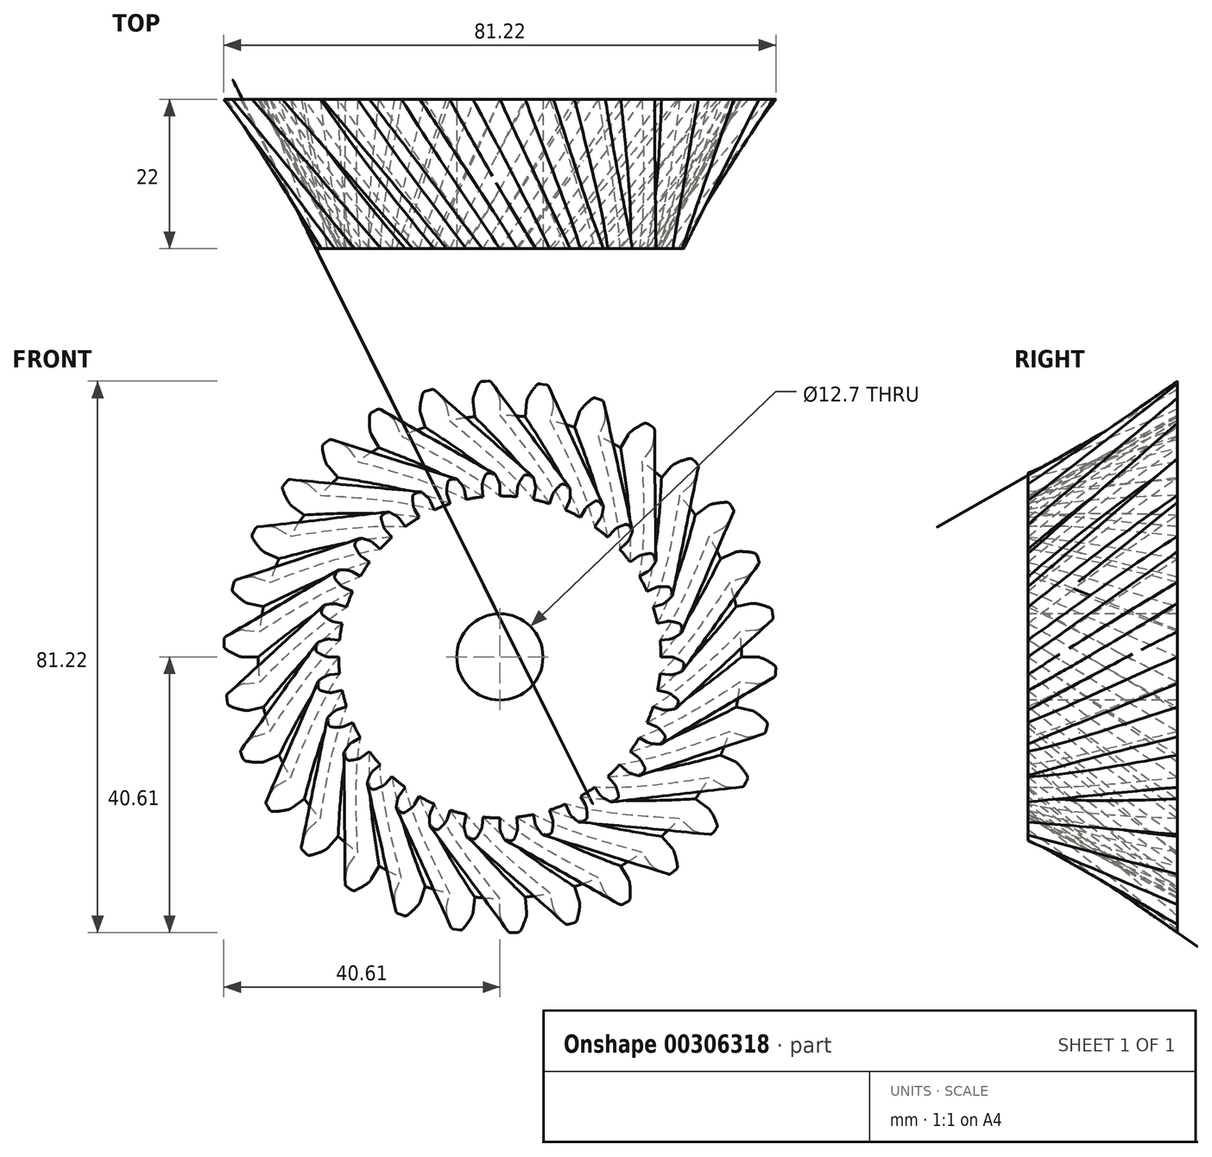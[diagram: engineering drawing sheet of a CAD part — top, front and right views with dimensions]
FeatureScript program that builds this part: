
annotation { "Feature Type Name" : "Feature", "Feature Type Description" : "" }
export const myFeature = defineFeature(function(context is Context, id is Id, definition is map)
    precondition{}
    {
        {
            var Q0;
            Q0=qCreatedBy(makeId("Front.planeOp"),FACE);
            var sketch = newSketch(context, id + "F0", { "sketchPlane" : qUnion([Q0])});
            skCircle(sketch, "E0", {"center": v(0, 0) * mm, "radius": 35.56 * mm});
            skArc(sketch, "E1.trimOffspring", {"start": v(-0.11, 38.4) * mm, "mid": v(-0.6, 39.43) * mm, "end": v(-1.21, 40.4) * mm});
            skLineSegment(sketch, "E2", {"start": v(0, 37.8) * mm, "end": v(0, 35.56) * mm});
            skLineSegment(sketch, "E3", {"start": v(-1.64, 40.6) * mm, "end": v(-2.13, 40.6) * mm});
            skLineSegment(sketch, "E4.MirrorCS", {"start": v(-2.61, 40.56) * mm, "end": v(-2.13, 40.6) * mm});
            skArc(sketch, "E5.MirrorCS", {"start": v(-3.9, 38.2) * mm, "mid": v(-3.52, 39.28) * mm, "end": v(-3.02, 40.3) * mm});
            skLineSegment(sketch, "E6.MirrorCS", {"start": v(-3.95, 37.6) * mm, "end": v(-3.72, 35.37) * mm});
            skPoint(sketch, "E7.visualSharp", {"position": v(-3.98, 37.9) * mm});
            skArc(sketch, "E7.filletArc", {"start": v(-3.9, 38.2) * mm, "mid": v(-3.95, 37.9) * mm, "end": v(-3.95, 37.6) * mm});
            skPoint(sketch, "E8.visualSharp", {"position": v(0, 38.1) * mm});
            skArc(sketch, "E8.filletArc", {"start": v(0, 37.8) * mm, "mid": v(-0.03, 38.1) * mm, "end": v(-0.11, 38.4) * mm});
            skPoint(sketch, "E9.visualSharp", {"position": v(-2.88, 40.54) * mm});
            skArc(sketch, "E9.filletArc", {"start": v(-2.61, 40.56) * mm, "mid": v(-2.85, 40.48) * mm, "end": v(-3.02, 40.3) * mm});
            skPoint(sketch, "E10.visualSharp", {"position": v(-1.38, 40.62) * mm});
            skArc(sketch, "E10.filletArc", {"start": v(-1.21, 40.4) * mm, "mid": v(-1.4, 40.56) * mm, "end": v(-1.64, 40.6) * mm});
            skLineSegment(sketch, "E11.1.0", {"start": v(-11.68, 35.96) * mm, "end": v(-10.99, 33.82) * mm});
            skArc(sketch, "E11.1.1", {"start": v(-11.76, 36.56) * mm, "mid": v(-11.75, 36.25) * mm, "end": v(-11.68, 35.96) * mm});
            skArc(sketch, "E11.1.2", {"start": v(-11.76, 36.56) * mm, "mid": v(-11.61, 37.69) * mm, "end": v(-11.33, 38.8) * mm});
            skArc(sketch, "E11.1.3", {"start": v(-10.99, 39.13) * mm, "mid": v(-11.2, 39) * mm, "end": v(-11.33, 38.8) * mm});
            skLineSegment(sketch, "E11.1.4", {"start": v(-10.99, 39.13) * mm, "end": v(-10.52, 39.26) * mm});
            skLineSegment(sketch, "E11.1.5", {"start": v(-10.05, 39.38) * mm, "end": v(-10.52, 39.26) * mm});
            skArc(sketch, "E11.1.6", {"start": v(-9.58, 39.26) * mm, "mid": v(-9.8, 39.38) * mm, "end": v(-10.05, 39.38) * mm});
            skArc(sketch, "E11.1.7", {"start": v(-8.1, 37.54) * mm, "mid": v(-8.79, 38.44) * mm, "end": v(-9.58, 39.26) * mm});
            skArc(sketch, "E11.1.8", {"start": v(-7.86, 36.98) * mm, "mid": v(-7.95, 37.27) * mm, "end": v(-8.1, 37.54) * mm});
            skLineSegment(sketch, "E11.1.9", {"start": v(-7.86, 36.98) * mm, "end": v(-7.4, 34.78) * mm});
            skLineSegment(sketch, "E11.2.0", {"start": v(-18.9, 32.74) * mm, "end": v(-17.78, 30.8) * mm});
            skArc(sketch, "E11.2.1", {"start": v(-19.1, 33.31) * mm, "mid": v(-19.03, 33.02) * mm, "end": v(-18.9, 32.74) * mm});
            skArc(sketch, "E11.2.2", {"start": v(-19.1, 33.31) * mm, "mid": v(-19.2, 34.45) * mm, "end": v(-19.15, 35.6) * mm});
            skArc(sketch, "E11.2.3", {"start": v(-18.88, 35.99) * mm, "mid": v(-19.06, 35.82) * mm, "end": v(-19.15, 35.6) * mm});
            skLineSegment(sketch, "E11.2.4", {"start": v(-18.88, 35.99) * mm, "end": v(-18.45, 36.22) * mm});
            skLineSegment(sketch, "E11.2.5", {"start": v(-18.02, 36.43) * mm, "end": v(-18.45, 36.22) * mm});
            skArc(sketch, "E11.2.6", {"start": v(-17.54, 36.41) * mm, "mid": v(-17.78, 36.48) * mm, "end": v(-18.02, 36.43) * mm});
            skArc(sketch, "E11.2.7", {"start": v(-15.72, 35.03) * mm, "mid": v(-16.59, 35.78) * mm, "end": v(-17.54, 36.41) * mm});
            skArc(sketch, "E11.2.8", {"start": v(-15.38, 34.54) * mm, "mid": v(-15.53, 34.8) * mm, "end": v(-15.72, 35.03) * mm});
            skLineSegment(sketch, "E11.2.9", {"start": v(-15.38, 34.54) * mm, "end": v(-14.46, 32.49) * mm});
            skLineSegment(sketch, "E11.3.0", {"start": v(-25.3, 28.1) * mm, "end": v(-23.8, 26.43) * mm});
            skArc(sketch, "E11.3.1", {"start": v(-25.6, 28.61) * mm, "mid": v(-25.48, 28.34) * mm, "end": v(-25.3, 28.1) * mm});
            skArc(sketch, "E11.3.2", {"start": v(-25.6, 28.61) * mm, "mid": v(-25.94, 29.7) * mm, "end": v(-26.13, 30.83) * mm});
            skArc(sketch, "E11.3.3", {"start": v(-25.95, 31.28) * mm, "mid": v(-26.1, 31.08) * mm, "end": v(-26.13, 30.83) * mm});
            skLineSegment(sketch, "E11.3.4", {"start": v(-25.95, 31.28) * mm, "end": v(-25.58, 31.59) * mm});
            skLineSegment(sketch, "E11.3.5", {"start": v(-25.2, 31.89) * mm, "end": v(-25.58, 31.59) * mm});
            skArc(sketch, "E11.3.6", {"start": v(-24.73, 31.97) * mm, "mid": v(-24.97, 31.99) * mm, "end": v(-25.2, 31.89) * mm});
            skArc(sketch, "E11.3.7", {"start": v(-22.66, 31) * mm, "mid": v(-23.67, 31.55) * mm, "end": v(-24.73, 31.97) * mm});
            skArc(sketch, "E11.3.8", {"start": v(-22.22, 30.59) * mm, "mid": v(-22.42, 30.81) * mm, "end": v(-22.66, 31) * mm});
            skLineSegment(sketch, "E11.3.9", {"start": v(-22.22, 30.59) * mm, "end": v(-20.9, 28.77) * mm});
            skLineSegment(sketch, "E11.4.0", {"start": v(-30.59, 22.22) * mm, "end": v(-28.77, 20.9) * mm});
            skArc(sketch, "E11.4.1", {"start": v(-31, 22.66) * mm, "mid": v(-30.81, 22.42) * mm, "end": v(-30.59, 22.22) * mm});
            skArc(sketch, "E11.4.2", {"start": v(-31, 22.66) * mm, "mid": v(-31.55, 23.67) * mm, "end": v(-31.97, 24.73) * mm});
            skArc(sketch, "E11.4.3", {"start": v(-31.89, 25.2) * mm, "mid": v(-31.99, 24.97) * mm, "end": v(-31.97, 24.73) * mm});
            skLineSegment(sketch, "E11.4.4", {"start": v(-31.89, 25.2) * mm, "end": v(-31.59, 25.58) * mm});
            skLineSegment(sketch, "E11.4.5", {"start": v(-31.28, 25.95) * mm, "end": v(-31.59, 25.58) * mm});
            skArc(sketch, "E11.4.6", {"start": v(-30.83, 26.13) * mm, "mid": v(-31.08, 26.1) * mm, "end": v(-31.28, 25.95) * mm});
            skArc(sketch, "E11.4.7", {"start": v(-28.61, 25.6) * mm, "mid": v(-29.7, 25.94) * mm, "end": v(-30.83, 26.13) * mm});
            skArc(sketch, "E11.4.8", {"start": v(-28.1, 25.3) * mm, "mid": v(-28.34, 25.48) * mm, "end": v(-28.61, 25.6) * mm});
            skLineSegment(sketch, "E11.4.9", {"start": v(-28.1, 25.3) * mm, "end": v(-26.43, 23.8) * mm});
            skLineSegment(sketch, "E11.5.0", {"start": v(-34.54, 15.38) * mm, "end": v(-32.49, 14.46) * mm});
            skArc(sketch, "E11.5.1", {"start": v(-35.03, 15.72) * mm, "mid": v(-34.8, 15.53) * mm, "end": v(-34.54, 15.38) * mm});
            skArc(sketch, "E11.5.2", {"start": v(-35.03, 15.72) * mm, "mid": v(-35.78, 16.59) * mm, "end": v(-36.41, 17.54) * mm});
            skArc(sketch, "E11.5.3", {"start": v(-36.43, 18.02) * mm, "mid": v(-36.48, 17.78) * mm, "end": v(-36.41, 17.54) * mm});
            skLineSegment(sketch, "E11.5.4", {"start": v(-36.43, 18.02) * mm, "end": v(-36.22, 18.45) * mm});
            skLineSegment(sketch, "E11.5.5", {"start": v(-35.99, 18.88) * mm, "end": v(-36.22, 18.45) * mm});
            skArc(sketch, "E11.5.6", {"start": v(-35.6, 19.15) * mm, "mid": v(-35.82, 19.06) * mm, "end": v(-35.99, 18.88) * mm});
            skArc(sketch, "E11.5.7", {"start": v(-33.31, 19.1) * mm, "mid": v(-34.45, 19.2) * mm, "end": v(-35.6, 19.15) * mm});
            skArc(sketch, "E11.5.8", {"start": v(-32.74, 18.9) * mm, "mid": v(-33.02, 19.03) * mm, "end": v(-33.31, 19.1) * mm});
            skLineSegment(sketch, "E11.5.9", {"start": v(-32.74, 18.9) * mm, "end": v(-30.8, 17.78) * mm});
            skLineSegment(sketch, "E11.6.0", {"start": v(-36.98, 7.86) * mm, "end": v(-34.78, 7.4) * mm});
            skArc(sketch, "E11.6.1", {"start": v(-37.54, 8.1) * mm, "mid": v(-37.27, 7.95) * mm, "end": v(-36.98, 7.86) * mm});
            skArc(sketch, "E11.6.2", {"start": v(-37.54, 8.1) * mm, "mid": v(-38.44, 8.79) * mm, "end": v(-39.26, 9.58) * mm});
            skArc(sketch, "E11.6.3", {"start": v(-39.38, 10.05) * mm, "mid": v(-39.38, 9.8) * mm, "end": v(-39.26, 9.58) * mm});
            skLineSegment(sketch, "E11.6.4", {"start": v(-39.38, 10.05) * mm, "end": v(-39.26, 10.52) * mm});
            skLineSegment(sketch, "E11.6.5", {"start": v(-39.13, 10.99) * mm, "end": v(-39.26, 10.52) * mm});
            skArc(sketch, "E11.6.6", {"start": v(-38.8, 11.33) * mm, "mid": v(-39, 11.2) * mm, "end": v(-39.13, 10.99) * mm});
            skArc(sketch, "E11.6.7", {"start": v(-36.56, 11.76) * mm, "mid": v(-37.69, 11.61) * mm, "end": v(-38.8, 11.33) * mm});
            skArc(sketch, "E11.6.8", {"start": v(-35.96, 11.68) * mm, "mid": v(-36.25, 11.75) * mm, "end": v(-36.56, 11.76) * mm});
            skLineSegment(sketch, "E11.6.9", {"start": v(-35.96, 11.68) * mm, "end": v(-33.82, 10.99) * mm});
            skLineSegment(sketch, "E11.7.0", {"start": v(-37.8, 0) * mm, "end": v(-35.56, 0) * mm});
            skArc(sketch, "E11.7.1", {"start": v(-38.4, 0.11) * mm, "mid": v(-38.1, 0.03) * mm, "end": v(-37.8, 0) * mm});
            skArc(sketch, "E11.7.2", {"start": v(-38.4, 0.11) * mm, "mid": v(-39.43, 0.6) * mm, "end": v(-40.4, 1.21) * mm});
            skArc(sketch, "E11.7.3", {"start": v(-40.6, 1.64) * mm, "mid": v(-40.56, 1.4) * mm, "end": v(-40.4, 1.21) * mm});
            skLineSegment(sketch, "E11.7.4", {"start": v(-40.6, 1.64) * mm, "end": v(-40.6, 2.13) * mm});
            skLineSegment(sketch, "E11.7.5", {"start": v(-40.56, 2.61) * mm, "end": v(-40.6, 2.13) * mm});
            skArc(sketch, "E11.7.6", {"start": v(-40.3, 3.02) * mm, "mid": v(-40.48, 2.85) * mm, "end": v(-40.56, 2.61) * mm});
            skArc(sketch, "E11.7.7", {"start": v(-38.2, 3.9) * mm, "mid": v(-39.28, 3.52) * mm, "end": v(-40.3, 3.02) * mm});
            skArc(sketch, "E11.7.8", {"start": v(-37.6, 3.95) * mm, "mid": v(-37.9, 3.95) * mm, "end": v(-38.2, 3.9) * mm});
            skLineSegment(sketch, "E11.7.9", {"start": v(-37.6, 3.95) * mm, "end": v(-35.37, 3.72) * mm});
            skLineSegment(sketch, "E11.8.0", {"start": v(-36.98, -7.86) * mm, "end": v(-34.78, -7.4) * mm});
            skArc(sketch, "E11.8.1", {"start": v(-37.58, -7.87) * mm, "mid": v(-37.28, -7.9) * mm, "end": v(-36.98, -7.86) * mm});
            skArc(sketch, "E11.8.2", {"start": v(-37.58, -7.87) * mm, "mid": v(-38.7, -7.6) * mm, "end": v(-39.77, -7.21) * mm});
            skArc(sketch, "E11.8.3", {"start": v(-40.06, -6.84) * mm, "mid": v(-39.96, -7.06) * mm, "end": v(-39.77, -7.21) * mm});
            skLineSegment(sketch, "E11.8.4", {"start": v(-40.06, -6.84) * mm, "end": v(-40.15, -6.36) * mm});
            skLineSegment(sketch, "E11.8.5", {"start": v(-40.21, -5.88) * mm, "end": v(-40.15, -6.36) * mm});
            skArc(sketch, "E11.8.6", {"start": v(-40.05, -5.43) * mm, "mid": v(-40.19, -5.63) * mm, "end": v(-40.21, -5.88) * mm});
            skArc(sketch, "E11.8.7", {"start": v(-38.18, -4.13) * mm, "mid": v(-39.15, -4.72) * mm, "end": v(-40.05, -5.43) * mm});
            skArc(sketch, "E11.8.8", {"start": v(-37.6, -3.95) * mm, "mid": v(-37.9, -4.01) * mm, "end": v(-38.18, -4.13) * mm});
            skLineSegment(sketch, "E11.8.9", {"start": v(-37.6, -3.95) * mm, "end": v(-35.37, -3.72) * mm});
            skLineSegment(sketch, "E11.9.0", {"start": v(-34.54, -15.38) * mm, "end": v(-32.49, -14.46) * mm});
            skArc(sketch, "E11.9.1", {"start": v(-35.13, -15.51) * mm, "mid": v(-34.83, -15.47) * mm, "end": v(-34.54, -15.38) * mm});
            skArc(sketch, "E11.9.2", {"start": v(-35.13, -15.51) * mm, "mid": v(-36.27, -15.49) * mm, "end": v(-37.4, -15.32) * mm});
            skArc(sketch, "E11.9.3", {"start": v(-37.76, -15.02) * mm, "mid": v(-37.62, -15.22) * mm, "end": v(-37.4, -15.32) * mm});
            skLineSegment(sketch, "E11.9.4", {"start": v(-37.76, -15.02) * mm, "end": v(-37.95, -14.57) * mm});
            skLineSegment(sketch, "E11.9.5", {"start": v(-38.11, -14.11) * mm, "end": v(-37.95, -14.57) * mm});
            skArc(sketch, "E11.9.6", {"start": v(-38.04, -13.64) * mm, "mid": v(-38.14, -13.86) * mm, "end": v(-38.11, -14.11) * mm});
            skArc(sketch, "E11.9.7", {"start": v(-36.48, -11.98) * mm, "mid": v(-37.31, -12.76) * mm, "end": v(-38.04, -13.64) * mm});
            skArc(sketch, "E11.9.8", {"start": v(-35.96, -11.68) * mm, "mid": v(-36.23, -11.8) * mm, "end": v(-36.48, -11.98) * mm});
            skLineSegment(sketch, "E11.9.9", {"start": v(-35.96, -11.68) * mm, "end": v(-33.82, -10.99) * mm});
            skLineSegment(sketch, "E11.10.0", {"start": v(-30.59, -22.22) * mm, "end": v(-28.77, -20.9) * mm});
            skArc(sketch, "E11.10.1", {"start": v(-31.13, -22.48) * mm, "mid": v(-30.85, -22.38) * mm, "end": v(-30.59, -22.22) * mm});
            skArc(sketch, "E11.10.2", {"start": v(-31.13, -22.48) * mm, "mid": v(-32.26, -22.69) * mm, "end": v(-33.4, -22.76) * mm});
            skArc(sketch, "E11.10.3", {"start": v(-33.82, -22.54) * mm, "mid": v(-33.63, -22.7) * mm, "end": v(-33.4, -22.76) * mm});
            skLineSegment(sketch, "E11.10.4", {"start": v(-33.82, -22.54) * mm, "end": v(-34.09, -22.14) * mm});
            skLineSegment(sketch, "E11.10.5", {"start": v(-34.35, -21.73) * mm, "end": v(-34.09, -22.14) * mm});
            skArc(sketch, "E11.10.6", {"start": v(-34.38, -21.25) * mm, "mid": v(-34.42, -21.5) * mm, "end": v(-34.35, -21.73) * mm});
            skArc(sketch, "E11.10.7", {"start": v(-33.2, -19.3) * mm, "mid": v(-33.85, -20.24) * mm, "end": v(-34.38, -21.25) * mm});
            skArc(sketch, "E11.10.8", {"start": v(-32.74, -18.9) * mm, "mid": v(-32.99, -19.08) * mm, "end": v(-33.2, -19.3) * mm});
            skLineSegment(sketch, "E11.10.9", {"start": v(-32.74, -18.9) * mm, "end": v(-30.8, -17.78) * mm});
            skLineSegment(sketch, "E11.11.0", {"start": v(-25.3, -28.1) * mm, "end": v(-23.8, -26.43) * mm});
            skArc(sketch, "E11.11.1", {"start": v(-25.78, -28.46) * mm, "mid": v(-25.52, -28.3) * mm, "end": v(-25.3, -28.1) * mm});
            skArc(sketch, "E11.11.2", {"start": v(-25.78, -28.46) * mm, "mid": v(-26.83, -28.9) * mm, "end": v(-27.93, -29.2) * mm});
            skArc(sketch, "E11.11.3", {"start": v(-28.4, -29.08) * mm, "mid": v(-28.18, -29.2) * mm, "end": v(-27.93, -29.2) * mm});
            skLineSegment(sketch, "E11.11.4", {"start": v(-28.4, -29.08) * mm, "end": v(-28.74, -28.74) * mm});
            skLineSegment(sketch, "E11.11.5", {"start": v(-29.08, -28.4) * mm, "end": v(-28.74, -28.74) * mm});
            skArc(sketch, "E11.11.6", {"start": v(-29.2, -27.93) * mm, "mid": v(-29.2, -28.18) * mm, "end": v(-29.08, -28.4) * mm});
            skArc(sketch, "E11.11.7", {"start": v(-28.46, -25.78) * mm, "mid": v(-28.9, -26.83) * mm, "end": v(-29.2, -27.93) * mm});
            skArc(sketch, "E11.11.8", {"start": v(-28.1, -25.3) * mm, "mid": v(-28.3, -25.52) * mm, "end": v(-28.46, -25.78) * mm});
            skLineSegment(sketch, "E11.11.9", {"start": v(-28.1, -25.3) * mm, "end": v(-26.43, -23.8) * mm});
            skLineSegment(sketch, "E11.12.0", {"start": v(-18.9, -32.74) * mm, "end": v(-17.78, -30.8) * mm});
            skArc(sketch, "E11.12.1", {"start": v(-19.3, -33.2) * mm, "mid": v(-19.08, -32.99) * mm, "end": v(-18.9, -32.74) * mm});
            skArc(sketch, "E11.12.2", {"start": v(-19.3, -33.2) * mm, "mid": v(-20.24, -33.85) * mm, "end": v(-21.25, -34.38) * mm});
            skArc(sketch, "E11.12.3", {"start": v(-21.73, -34.35) * mm, "mid": v(-21.5, -34.42) * mm, "end": v(-21.25, -34.38) * mm});
            skLineSegment(sketch, "E11.12.4", {"start": v(-21.73, -34.35) * mm, "end": v(-22.14, -34.09) * mm});
            skLineSegment(sketch, "E11.12.5", {"start": v(-22.54, -33.82) * mm, "end": v(-22.14, -34.09) * mm});
            skArc(sketch, "E11.12.6", {"start": v(-22.76, -33.4) * mm, "mid": v(-22.7, -33.63) * mm, "end": v(-22.54, -33.82) * mm});
            skArc(sketch, "E11.12.7", {"start": v(-22.48, -31.13) * mm, "mid": v(-22.69, -32.26) * mm, "end": v(-22.76, -33.4) * mm});
            skArc(sketch, "E11.12.8", {"start": v(-22.22, -30.59) * mm, "mid": v(-22.38, -30.85) * mm, "end": v(-22.48, -31.13) * mm});
            skLineSegment(sketch, "E11.12.9", {"start": v(-22.22, -30.59) * mm, "end": v(-20.9, -28.77) * mm});
            skLineSegment(sketch, "E11.13.0", {"start": v(-11.68, -35.96) * mm, "end": v(-10.99, -33.82) * mm});
            skArc(sketch, "E11.13.1", {"start": v(-11.98, -36.48) * mm, "mid": v(-11.8, -36.23) * mm, "end": v(-11.68, -35.96) * mm});
            skArc(sketch, "E11.13.2", {"start": v(-11.98, -36.48) * mm, "mid": v(-12.76, -37.31) * mm, "end": v(-13.64, -38.04) * mm});
            skArc(sketch, "E11.13.3", {"start": v(-14.11, -38.11) * mm, "mid": v(-13.86, -38.14) * mm, "end": v(-13.64, -38.04) * mm});
            skLineSegment(sketch, "E11.13.4", {"start": v(-14.11, -38.11) * mm, "end": v(-14.57, -37.95) * mm});
            skLineSegment(sketch, "E11.13.5", {"start": v(-15.02, -37.76) * mm, "end": v(-14.57, -37.95) * mm});
            skArc(sketch, "E11.13.6", {"start": v(-15.32, -37.4) * mm, "mid": v(-15.22, -37.62) * mm, "end": v(-15.02, -37.76) * mm});
            skArc(sketch, "E11.13.7", {"start": v(-15.51, -35.13) * mm, "mid": v(-15.49, -36.27) * mm, "end": v(-15.32, -37.4) * mm});
            skArc(sketch, "E11.13.8", {"start": v(-15.38, -34.54) * mm, "mid": v(-15.47, -34.83) * mm, "end": v(-15.51, -35.13) * mm});
            skLineSegment(sketch, "E11.13.9", {"start": v(-15.38, -34.54) * mm, "end": v(-14.46, -32.49) * mm});
            skLineSegment(sketch, "E11.14.0", {"start": v(-3.95, -37.6) * mm, "end": v(-3.72, -35.37) * mm});
            skArc(sketch, "E11.14.1", {"start": v(-4.13, -38.18) * mm, "mid": v(-4.01, -37.9) * mm, "end": v(-3.95, -37.6) * mm});
            skArc(sketch, "E11.14.2", {"start": v(-4.13, -38.18) * mm, "mid": v(-4.72, -39.15) * mm, "end": v(-5.43, -40.05) * mm});
            skArc(sketch, "E11.14.3", {"start": v(-5.88, -40.21) * mm, "mid": v(-5.63, -40.19) * mm, "end": v(-5.43, -40.05) * mm});
            skLineSegment(sketch, "E11.14.4", {"start": v(-5.88, -40.21) * mm, "end": v(-6.36, -40.15) * mm});
            skLineSegment(sketch, "E11.14.5", {"start": v(-6.84, -40.06) * mm, "end": v(-6.36, -40.15) * mm});
            skArc(sketch, "E11.14.6", {"start": v(-7.21, -39.77) * mm, "mid": v(-7.06, -39.96) * mm, "end": v(-6.84, -40.06) * mm});
            skArc(sketch, "E11.14.7", {"start": v(-7.87, -37.58) * mm, "mid": v(-7.6, -38.7) * mm, "end": v(-7.21, -39.77) * mm});
            skArc(sketch, "E11.14.8", {"start": v(-7.86, -36.98) * mm, "mid": v(-7.9, -37.28) * mm, "end": v(-7.87, -37.58) * mm});
            skLineSegment(sketch, "E11.14.9", {"start": v(-7.86, -36.98) * mm, "end": v(-7.4, -34.78) * mm});
            skLineSegment(sketch, "E11.15.0", {"start": v(3.95, -37.6) * mm, "end": v(3.72, -35.37) * mm});
            skArc(sketch, "E11.15.1", {"start": v(3.9, -38.2) * mm, "mid": v(3.95, -37.9) * mm, "end": v(3.95, -37.6) * mm});
            skArc(sketch, "E11.15.2", {"start": v(3.9, -38.2) * mm, "mid": v(3.52, -39.28) * mm, "end": v(3.02, -40.3) * mm});
            skArc(sketch, "E11.15.3", {"start": v(2.61, -40.56) * mm, "mid": v(2.85, -40.48) * mm, "end": v(3.02, -40.3) * mm});
            skLineSegment(sketch, "E11.15.4", {"start": v(2.61, -40.56) * mm, "end": v(2.13, -40.6) * mm});
            skLineSegment(sketch, "E11.15.5", {"start": v(1.64, -40.6) * mm, "end": v(2.13, -40.6) * mm});
            skArc(sketch, "E11.15.6", {"start": v(1.21, -40.4) * mm, "mid": v(1.4, -40.56) * mm, "end": v(1.64, -40.6) * mm});
            skArc(sketch, "E11.15.7", {"start": v(0.11, -38.4) * mm, "mid": v(0.6, -39.43) * mm, "end": v(1.21, -40.4) * mm});
            skArc(sketch, "E11.15.8", {"start": v(0, -37.8) * mm, "mid": v(0.03, -38.1) * mm, "end": v(0.11, -38.4) * mm});
            skLineSegment(sketch, "E11.15.9", {"start": v(0, -37.8) * mm, "end": v(0, -35.56) * mm});
            skLineSegment(sketch, "E11.16.0", {"start": v(11.68, -35.96) * mm, "end": v(10.99, -33.82) * mm});
            skArc(sketch, "E11.16.1", {"start": v(11.76, -36.56) * mm, "mid": v(11.75, -36.25) * mm, "end": v(11.68, -35.96) * mm});
            skArc(sketch, "E11.16.2", {"start": v(11.76, -36.56) * mm, "mid": v(11.61, -37.69) * mm, "end": v(11.33, -38.8) * mm});
            skArc(sketch, "E11.16.3", {"start": v(10.99, -39.13) * mm, "mid": v(11.2, -39) * mm, "end": v(11.33, -38.8) * mm});
            skLineSegment(sketch, "E11.16.4", {"start": v(10.99, -39.13) * mm, "end": v(10.52, -39.26) * mm});
            skLineSegment(sketch, "E11.16.5", {"start": v(10.05, -39.38) * mm, "end": v(10.52, -39.26) * mm});
            skArc(sketch, "E11.16.6", {"start": v(9.58, -39.26) * mm, "mid": v(9.8, -39.38) * mm, "end": v(10.05, -39.38) * mm});
            skArc(sketch, "E11.16.7", {"start": v(8.1, -37.54) * mm, "mid": v(8.79, -38.44) * mm, "end": v(9.58, -39.26) * mm});
            skArc(sketch, "E11.16.8", {"start": v(7.86, -36.98) * mm, "mid": v(7.95, -37.27) * mm, "end": v(8.1, -37.54) * mm});
            skLineSegment(sketch, "E11.16.9", {"start": v(7.86, -36.98) * mm, "end": v(7.4, -34.78) * mm});
            skLineSegment(sketch, "E11.17.0", {"start": v(18.9, -32.74) * mm, "end": v(17.78, -30.8) * mm});
            skArc(sketch, "E11.17.1", {"start": v(19.1, -33.31) * mm, "mid": v(19.03, -33.02) * mm, "end": v(18.9, -32.74) * mm});
            skArc(sketch, "E11.17.2", {"start": v(19.1, -33.31) * mm, "mid": v(19.2, -34.45) * mm, "end": v(19.15, -35.6) * mm});
            skArc(sketch, "E11.17.3", {"start": v(18.88, -35.99) * mm, "mid": v(19.06, -35.82) * mm, "end": v(19.15, -35.6) * mm});
            skLineSegment(sketch, "E11.17.4", {"start": v(18.88, -35.99) * mm, "end": v(18.45, -36.22) * mm});
            skLineSegment(sketch, "E11.17.5", {"start": v(18.02, -36.43) * mm, "end": v(18.45, -36.22) * mm});
            skArc(sketch, "E11.17.6", {"start": v(17.54, -36.41) * mm, "mid": v(17.78, -36.48) * mm, "end": v(18.02, -36.43) * mm});
            skArc(sketch, "E11.17.7", {"start": v(15.72, -35.03) * mm, "mid": v(16.59, -35.78) * mm, "end": v(17.54, -36.41) * mm});
            skArc(sketch, "E11.17.8", {"start": v(15.38, -34.54) * mm, "mid": v(15.53, -34.8) * mm, "end": v(15.72, -35.03) * mm});
            skLineSegment(sketch, "E11.17.9", {"start": v(15.38, -34.54) * mm, "end": v(14.46, -32.49) * mm});
            skLineSegment(sketch, "E11.18.0", {"start": v(25.3, -28.1) * mm, "end": v(23.8, -26.43) * mm});
            skArc(sketch, "E11.18.1", {"start": v(25.6, -28.61) * mm, "mid": v(25.48, -28.34) * mm, "end": v(25.3, -28.1) * mm});
            skArc(sketch, "E11.18.2", {"start": v(25.6, -28.61) * mm, "mid": v(25.94, -29.7) * mm, "end": v(26.13, -30.83) * mm});
            skArc(sketch, "E11.18.3", {"start": v(25.95, -31.28) * mm, "mid": v(26.1, -31.08) * mm, "end": v(26.13, -30.83) * mm});
            skLineSegment(sketch, "E11.18.4", {"start": v(25.95, -31.28) * mm, "end": v(25.58, -31.59) * mm});
            skLineSegment(sketch, "E11.18.5", {"start": v(25.2, -31.89) * mm, "end": v(25.58, -31.59) * mm});
            skArc(sketch, "E11.18.6", {"start": v(24.73, -31.97) * mm, "mid": v(24.97, -31.99) * mm, "end": v(25.2, -31.89) * mm});
            skArc(sketch, "E11.18.7", {"start": v(22.66, -31) * mm, "mid": v(23.67, -31.55) * mm, "end": v(24.73, -31.97) * mm});
            skArc(sketch, "E11.18.8", {"start": v(22.22, -30.59) * mm, "mid": v(22.42, -30.81) * mm, "end": v(22.66, -31) * mm});
            skLineSegment(sketch, "E11.18.9", {"start": v(22.22, -30.59) * mm, "end": v(20.9, -28.77) * mm});
            skLineSegment(sketch, "E11.19.0", {"start": v(30.59, -22.22) * mm, "end": v(28.77, -20.9) * mm});
            skArc(sketch, "E11.19.1", {"start": v(31, -22.66) * mm, "mid": v(30.81, -22.42) * mm, "end": v(30.59, -22.22) * mm});
            skArc(sketch, "E11.19.2", {"start": v(31, -22.66) * mm, "mid": v(31.55, -23.67) * mm, "end": v(31.97, -24.73) * mm});
            skArc(sketch, "E11.19.3", {"start": v(31.89, -25.2) * mm, "mid": v(31.99, -24.97) * mm, "end": v(31.97, -24.73) * mm});
            skLineSegment(sketch, "E11.19.4", {"start": v(31.89, -25.2) * mm, "end": v(31.59, -25.58) * mm});
            skLineSegment(sketch, "E11.19.5", {"start": v(31.28, -25.95) * mm, "end": v(31.59, -25.58) * mm});
            skArc(sketch, "E11.19.6", {"start": v(30.83, -26.13) * mm, "mid": v(31.08, -26.1) * mm, "end": v(31.28, -25.95) * mm});
            skArc(sketch, "E11.19.7", {"start": v(28.61, -25.6) * mm, "mid": v(29.7, -25.94) * mm, "end": v(30.83, -26.13) * mm});
            skArc(sketch, "E11.19.8", {"start": v(28.1, -25.3) * mm, "mid": v(28.34, -25.48) * mm, "end": v(28.61, -25.6) * mm});
            skLineSegment(sketch, "E11.19.9", {"start": v(28.1, -25.3) * mm, "end": v(26.43, -23.8) * mm});
            skLineSegment(sketch, "E11.20.0", {"start": v(34.54, -15.38) * mm, "end": v(32.49, -14.46) * mm});
            skArc(sketch, "E11.20.1", {"start": v(35.03, -15.72) * mm, "mid": v(34.8, -15.53) * mm, "end": v(34.54, -15.38) * mm});
            skArc(sketch, "E11.20.2", {"start": v(35.03, -15.72) * mm, "mid": v(35.78, -16.59) * mm, "end": v(36.41, -17.54) * mm});
            skArc(sketch, "E11.20.3", {"start": v(36.43, -18.02) * mm, "mid": v(36.48, -17.78) * mm, "end": v(36.41, -17.54) * mm});
            skLineSegment(sketch, "E11.20.4", {"start": v(36.43, -18.02) * mm, "end": v(36.22, -18.45) * mm});
            skLineSegment(sketch, "E11.20.5", {"start": v(35.99, -18.88) * mm, "end": v(36.22, -18.45) * mm});
            skArc(sketch, "E11.20.6", {"start": v(35.6, -19.15) * mm, "mid": v(35.82, -19.06) * mm, "end": v(35.99, -18.88) * mm});
            skArc(sketch, "E11.20.7", {"start": v(33.31, -19.1) * mm, "mid": v(34.45, -19.2) * mm, "end": v(35.6, -19.15) * mm});
            skArc(sketch, "E11.20.8", {"start": v(32.74, -18.9) * mm, "mid": v(33.02, -19.03) * mm, "end": v(33.31, -19.1) * mm});
            skLineSegment(sketch, "E11.20.9", {"start": v(32.74, -18.9) * mm, "end": v(30.8, -17.78) * mm});
            skLineSegment(sketch, "E11.21.0", {"start": v(36.98, -7.86) * mm, "end": v(34.78, -7.4) * mm});
            skArc(sketch, "E11.21.1", {"start": v(37.54, -8.1) * mm, "mid": v(37.27, -7.95) * mm, "end": v(36.98, -7.86) * mm});
            skArc(sketch, "E11.21.2", {"start": v(37.54, -8.1) * mm, "mid": v(38.44, -8.79) * mm, "end": v(39.26, -9.58) * mm});
            skArc(sketch, "E11.21.3", {"start": v(39.38, -10.05) * mm, "mid": v(39.38, -9.8) * mm, "end": v(39.26, -9.58) * mm});
            skLineSegment(sketch, "E11.21.4", {"start": v(39.38, -10.05) * mm, "end": v(39.26, -10.52) * mm});
            skLineSegment(sketch, "E11.21.5", {"start": v(39.13, -10.99) * mm, "end": v(39.26, -10.52) * mm});
            skArc(sketch, "E11.21.6", {"start": v(38.8, -11.33) * mm, "mid": v(39, -11.2) * mm, "end": v(39.13, -10.99) * mm});
            skArc(sketch, "E11.21.7", {"start": v(36.56, -11.76) * mm, "mid": v(37.69, -11.61) * mm, "end": v(38.8, -11.33) * mm});
            skArc(sketch, "E11.21.8", {"start": v(35.96, -11.68) * mm, "mid": v(36.25, -11.75) * mm, "end": v(36.56, -11.76) * mm});
            skLineSegment(sketch, "E11.21.9", {"start": v(35.96, -11.68) * mm, "end": v(33.82, -10.99) * mm});
            skLineSegment(sketch, "E11.22.0", {"start": v(37.8, 0) * mm, "end": v(35.56, 0) * mm});
            skArc(sketch, "E11.22.1", {"start": v(38.4, -0.11) * mm, "mid": v(38.1, -0.03) * mm, "end": v(37.8, 0) * mm});
            skArc(sketch, "E11.22.2", {"start": v(38.4, -0.11) * mm, "mid": v(39.43, -0.6) * mm, "end": v(40.4, -1.21) * mm});
            skArc(sketch, "E11.22.3", {"start": v(40.6, -1.64) * mm, "mid": v(40.56, -1.4) * mm, "end": v(40.4, -1.21) * mm});
            skLineSegment(sketch, "E11.22.4", {"start": v(40.6, -1.64) * mm, "end": v(40.6, -2.13) * mm});
            skLineSegment(sketch, "E11.22.5", {"start": v(40.56, -2.61) * mm, "end": v(40.6, -2.13) * mm});
            skArc(sketch, "E11.22.6", {"start": v(40.3, -3.02) * mm, "mid": v(40.48, -2.85) * mm, "end": v(40.56, -2.61) * mm});
            skArc(sketch, "E11.22.7", {"start": v(38.2, -3.9) * mm, "mid": v(39.28, -3.52) * mm, "end": v(40.3, -3.02) * mm});
            skArc(sketch, "E11.22.8", {"start": v(37.6, -3.95) * mm, "mid": v(37.9, -3.95) * mm, "end": v(38.2, -3.9) * mm});
            skLineSegment(sketch, "E11.22.9", {"start": v(37.6, -3.95) * mm, "end": v(35.37, -3.72) * mm});
            skLineSegment(sketch, "E11.23.0", {"start": v(36.98, 7.86) * mm, "end": v(34.78, 7.4) * mm});
            skArc(sketch, "E11.23.1", {"start": v(37.58, 7.87) * mm, "mid": v(37.28, 7.9) * mm, "end": v(36.98, 7.86) * mm});
            skArc(sketch, "E11.23.2", {"start": v(37.58, 7.87) * mm, "mid": v(38.7, 7.6) * mm, "end": v(39.77, 7.21) * mm});
            skArc(sketch, "E11.23.3", {"start": v(40.06, 6.84) * mm, "mid": v(39.96, 7.06) * mm, "end": v(39.77, 7.21) * mm});
            skLineSegment(sketch, "E11.23.4", {"start": v(40.06, 6.84) * mm, "end": v(40.15, 6.36) * mm});
            skLineSegment(sketch, "E11.23.5", {"start": v(40.21, 5.88) * mm, "end": v(40.15, 6.36) * mm});
            skArc(sketch, "E11.23.6", {"start": v(40.05, 5.43) * mm, "mid": v(40.19, 5.63) * mm, "end": v(40.21, 5.88) * mm});
            skArc(sketch, "E11.23.7", {"start": v(38.18, 4.13) * mm, "mid": v(39.15, 4.72) * mm, "end": v(40.05, 5.43) * mm});
            skArc(sketch, "E11.23.8", {"start": v(37.6, 3.95) * mm, "mid": v(37.9, 4.01) * mm, "end": v(38.18, 4.13) * mm});
            skLineSegment(sketch, "E11.23.9", {"start": v(37.6, 3.95) * mm, "end": v(35.37, 3.72) * mm});
            skLineSegment(sketch, "E11.24.0", {"start": v(34.54, 15.38) * mm, "end": v(32.49, 14.46) * mm});
            skArc(sketch, "E11.24.1", {"start": v(35.13, 15.51) * mm, "mid": v(34.83, 15.47) * mm, "end": v(34.54, 15.38) * mm});
            skArc(sketch, "E11.24.2", {"start": v(35.13, 15.51) * mm, "mid": v(36.27, 15.49) * mm, "end": v(37.4, 15.32) * mm});
            skArc(sketch, "E11.24.3", {"start": v(37.76, 15.02) * mm, "mid": v(37.62, 15.22) * mm, "end": v(37.4, 15.32) * mm});
            skLineSegment(sketch, "E11.24.4", {"start": v(37.76, 15.02) * mm, "end": v(37.95, 14.57) * mm});
            skLineSegment(sketch, "E11.24.5", {"start": v(38.11, 14.11) * mm, "end": v(37.95, 14.57) * mm});
            skArc(sketch, "E11.24.6", {"start": v(38.04, 13.64) * mm, "mid": v(38.14, 13.86) * mm, "end": v(38.11, 14.11) * mm});
            skArc(sketch, "E11.24.7", {"start": v(36.48, 11.98) * mm, "mid": v(37.31, 12.76) * mm, "end": v(38.04, 13.64) * mm});
            skArc(sketch, "E11.24.8", {"start": v(35.96, 11.68) * mm, "mid": v(36.23, 11.8) * mm, "end": v(36.48, 11.98) * mm});
            skLineSegment(sketch, "E11.24.9", {"start": v(35.96, 11.68) * mm, "end": v(33.82, 10.99) * mm});
            skLineSegment(sketch, "E11.25.0", {"start": v(30.59, 22.22) * mm, "end": v(28.77, 20.9) * mm});
            skArc(sketch, "E11.25.1", {"start": v(31.13, 22.48) * mm, "mid": v(30.85, 22.38) * mm, "end": v(30.59, 22.22) * mm});
            skArc(sketch, "E11.25.2", {"start": v(31.13, 22.48) * mm, "mid": v(32.26, 22.69) * mm, "end": v(33.4, 22.76) * mm});
            skArc(sketch, "E11.25.3", {"start": v(33.82, 22.54) * mm, "mid": v(33.63, 22.7) * mm, "end": v(33.4, 22.76) * mm});
            skLineSegment(sketch, "E11.25.4", {"start": v(33.82, 22.54) * mm, "end": v(34.09, 22.14) * mm});
            skLineSegment(sketch, "E11.25.5", {"start": v(34.35, 21.73) * mm, "end": v(34.09, 22.14) * mm});
            skArc(sketch, "E11.25.6", {"start": v(34.38, 21.25) * mm, "mid": v(34.42, 21.5) * mm, "end": v(34.35, 21.73) * mm});
            skArc(sketch, "E11.25.7", {"start": v(33.2, 19.3) * mm, "mid": v(33.85, 20.24) * mm, "end": v(34.38, 21.25) * mm});
            skArc(sketch, "E11.25.8", {"start": v(32.74, 18.9) * mm, "mid": v(32.99, 19.08) * mm, "end": v(33.2, 19.3) * mm});
            skLineSegment(sketch, "E11.25.9", {"start": v(32.74, 18.9) * mm, "end": v(30.8, 17.78) * mm});
            skLineSegment(sketch, "E11.26.0", {"start": v(25.3, 28.1) * mm, "end": v(23.8, 26.43) * mm});
            skArc(sketch, "E11.26.1", {"start": v(25.78, 28.46) * mm, "mid": v(25.52, 28.3) * mm, "end": v(25.3, 28.1) * mm});
            skArc(sketch, "E11.26.2", {"start": v(25.78, 28.46) * mm, "mid": v(26.83, 28.9) * mm, "end": v(27.93, 29.2) * mm});
            skArc(sketch, "E11.26.3", {"start": v(28.4, 29.08) * mm, "mid": v(28.18, 29.2) * mm, "end": v(27.93, 29.2) * mm});
            skLineSegment(sketch, "E11.26.4", {"start": v(28.4, 29.08) * mm, "end": v(28.74, 28.74) * mm});
            skLineSegment(sketch, "E11.26.5", {"start": v(29.08, 28.4) * mm, "end": v(28.74, 28.74) * mm});
            skArc(sketch, "E11.26.6", {"start": v(29.2, 27.93) * mm, "mid": v(29.2, 28.18) * mm, "end": v(29.08, 28.4) * mm});
            skArc(sketch, "E11.26.7", {"start": v(28.46, 25.78) * mm, "mid": v(28.9, 26.83) * mm, "end": v(29.2, 27.93) * mm});
            skArc(sketch, "E11.26.8", {"start": v(28.1, 25.3) * mm, "mid": v(28.3, 25.52) * mm, "end": v(28.46, 25.78) * mm});
            skLineSegment(sketch, "E11.26.9", {"start": v(28.1, 25.3) * mm, "end": v(26.43, 23.8) * mm});
            skLineSegment(sketch, "E11.27.0", {"start": v(18.9, 32.74) * mm, "end": v(17.78, 30.8) * mm});
            skArc(sketch, "E11.27.1", {"start": v(19.3, 33.2) * mm, "mid": v(19.08, 32.99) * mm, "end": v(18.9, 32.74) * mm});
            skArc(sketch, "E11.27.2", {"start": v(19.3, 33.2) * mm, "mid": v(20.24, 33.85) * mm, "end": v(21.25, 34.38) * mm});
            skArc(sketch, "E11.27.3", {"start": v(21.73, 34.35) * mm, "mid": v(21.5, 34.42) * mm, "end": v(21.25, 34.38) * mm});
            skLineSegment(sketch, "E11.27.4", {"start": v(21.73, 34.35) * mm, "end": v(22.14, 34.09) * mm});
            skLineSegment(sketch, "E11.27.5", {"start": v(22.54, 33.82) * mm, "end": v(22.14, 34.09) * mm});
            skArc(sketch, "E11.27.6", {"start": v(22.76, 33.4) * mm, "mid": v(22.7, 33.63) * mm, "end": v(22.54, 33.82) * mm});
            skArc(sketch, "E11.27.7", {"start": v(22.48, 31.13) * mm, "mid": v(22.69, 32.26) * mm, "end": v(22.76, 33.4) * mm});
            skArc(sketch, "E11.27.8", {"start": v(22.22, 30.59) * mm, "mid": v(22.38, 30.85) * mm, "end": v(22.48, 31.13) * mm});
            skLineSegment(sketch, "E11.27.9", {"start": v(22.22, 30.59) * mm, "end": v(20.9, 28.77) * mm});
            skLineSegment(sketch, "E11.28.0", {"start": v(11.68, 35.96) * mm, "end": v(10.99, 33.82) * mm});
            skArc(sketch, "E11.28.1", {"start": v(11.98, 36.48) * mm, "mid": v(11.8, 36.23) * mm, "end": v(11.68, 35.96) * mm});
            skArc(sketch, "E11.28.2", {"start": v(11.98, 36.48) * mm, "mid": v(12.76, 37.31) * mm, "end": v(13.64, 38.04) * mm});
            skArc(sketch, "E11.28.3", {"start": v(14.11, 38.11) * mm, "mid": v(13.86, 38.14) * mm, "end": v(13.64, 38.04) * mm});
            skLineSegment(sketch, "E11.28.4", {"start": v(14.11, 38.11) * mm, "end": v(14.57, 37.95) * mm});
            skLineSegment(sketch, "E11.28.5", {"start": v(15.02, 37.76) * mm, "end": v(14.57, 37.95) * mm});
            skArc(sketch, "E11.28.6", {"start": v(15.32, 37.4) * mm, "mid": v(15.22, 37.62) * mm, "end": v(15.02, 37.76) * mm});
            skArc(sketch, "E11.28.7", {"start": v(15.51, 35.13) * mm, "mid": v(15.49, 36.27) * mm, "end": v(15.32, 37.4) * mm});
            skArc(sketch, "E11.28.8", {"start": v(15.38, 34.54) * mm, "mid": v(15.47, 34.83) * mm, "end": v(15.51, 35.13) * mm});
            skLineSegment(sketch, "E11.28.9", {"start": v(15.38, 34.54) * mm, "end": v(14.46, 32.49) * mm});
            skLineSegment(sketch, "E11.29.0", {"start": v(3.95, 37.6) * mm, "end": v(3.72, 35.37) * mm});
            skArc(sketch, "E11.29.1", {"start": v(4.13, 38.18) * mm, "mid": v(4.01, 37.9) * mm, "end": v(3.95, 37.6) * mm});
            skArc(sketch, "E11.29.2", {"start": v(4.13, 38.18) * mm, "mid": v(4.72, 39.15) * mm, "end": v(5.43, 40.05) * mm});
            skArc(sketch, "E11.29.3", {"start": v(5.88, 40.21) * mm, "mid": v(5.63, 40.19) * mm, "end": v(5.43, 40.05) * mm});
            skLineSegment(sketch, "E11.29.4", {"start": v(5.88, 40.21) * mm, "end": v(6.36, 40.15) * mm});
            skLineSegment(sketch, "E11.29.5", {"start": v(6.84, 40.06) * mm, "end": v(6.36, 40.15) * mm});
            skArc(sketch, "E11.29.6", {"start": v(7.21, 39.77) * mm, "mid": v(7.06, 39.96) * mm, "end": v(6.84, 40.06) * mm});
            skArc(sketch, "E11.29.7", {"start": v(7.87, 37.58) * mm, "mid": v(7.6, 38.7) * mm, "end": v(7.21, 39.77) * mm});
            skArc(sketch, "E11.29.8", {"start": v(7.86, 36.98) * mm, "mid": v(7.9, 37.28) * mm, "end": v(7.87, 37.58) * mm});
            skLineSegment(sketch, "E11.29.9", {"start": v(7.86, 36.98) * mm, "end": v(7.4, 34.78) * mm});
            skSolve(sketch);
        }
        {
            var Q0;
            {var subQ0=sQuery(id+"F0.wireOp",EDGE,"E0");var subQ33=makeQuery(id+"F0.imprint","INTERSECT",VERTEX,{"derivedFrom":[subQ0,sQuery(id+"F0.wireOp",EDGE,"E11.22.0")]});Q0=makeQuery(id+"F0.imprint","IMPRINT",FACE,{"disambiguationData":[TD([[makeQuery(id+"F0.imprint","IMPRINT",EDGE,{"disambiguationData":[TD([[subQ33,-1.0]])],"derivedFrom":subQ0}),1.0]])]});}
            cPlane(context, id + "F1", {"entities" : qUnion([Q0]), "cplaneType" : CPlaneType.OFFSET, "offset" : 22 * mm, "width" : 152.4 * mm, "height" : 152.4 * mm});
        }
        {
            var Q0;
            Q0=qCreatedBy(id+"F1.planeOp",FACE);
            var sketch = newSketch(context, id + "F2", { "sketchPlane" : qUnion([Q0])});
            skCircle(sketch, "E12", {"center": v(0, 0) * mm, "radius": 23.71 * mm});
            skArc(sketch, "E13.trimOffspring", {"start": v(-0.11, 25.7) * mm, "mid": v(-0.36, 26.26) * mm, "end": v(-0.65, 26.8) * mm});
            skLineSegment(sketch, "E14", {"start": v(-1.1, 27.07) * mm, "end": v(-1.42, 27.06) * mm});
            skLineSegment(sketch, "E15", {"start": v(0, 25.1) * mm, "end": v(0, 23.71) * mm});
            skLineSegment(sketch, "E16.MirrorCS", {"start": v(-1.73, 27.04) * mm, "end": v(-1.42, 27.06) * mm});
            skArc(sketch, "E17.MirrorCS", {"start": v(-2.57, 25.57) * mm, "mid": v(-2.38, 26.16) * mm, "end": v(-2.16, 26.73) * mm});
            skLineSegment(sketch, "E18.MirrorCS", {"start": v(-2.62, 24.97) * mm, "end": v(-2.48, 23.58) * mm});
            skPoint(sketch, "E19.visualSharp", {"position": v(-2.66, 25.26) * mm});
            skArc(sketch, "E19.filletArc", {"start": v(-2.57, 25.57) * mm, "mid": v(-2.63, 25.27) * mm, "end": v(-2.62, 24.97) * mm});
            skPoint(sketch, "E20.visualSharp", {"position": v(0, 25.4) * mm});
            skArc(sketch, "E20.filletArc", {"start": v(0, 25.1) * mm, "mid": v(-0.03, 25.4) * mm, "end": v(-0.11, 25.7) * mm});
            skPoint(sketch, "E21.visualSharp", {"position": v(-2.03, 27.01) * mm});
            skArc(sketch, "E21.filletArc", {"start": v(-1.73, 27.04) * mm, "mid": v(-1.99, 26.94) * mm, "end": v(-2.16, 26.73) * mm});
            skPoint(sketch, "E22.visualSharp", {"position": v(-0.8, 27.08) * mm});
            skArc(sketch, "E22.filletArc", {"start": v(-0.65, 26.8) * mm, "mid": v(-0.84, 27) * mm, "end": v(-1.1, 27.07) * mm});
            skSolve(sketch);
        }
        {
            var Q0;
            Q0=makeQuery(id+"F2.imprint","IMPRINT",FACE,{"disambiguationData":[TD([[makeQuery(id+"F2.imprint","IMPRINT",EDGE,{"derivedFrom":sQuery(id+"F2.wireOp",EDGE,"E13.trimOffspring")}),1.0]])]});
            var Q1;
            {var subQ0=sQuery(id+"F0.wireOp",EDGE,"E11.2.0");Q1=makeQuery(id+"F0.imprint","IMPRINT",FACE,{"disambiguationData":[TD([[makeQuery(id+"F0.imprint","IMPRINT",EDGE,{"derivedFrom":subQ0}),1.0]])]});}
            loft(context, id + "F3", {"sheetProfilesArray" : [{ "sheetProfileEntities" : qUnion([Q0]) }, { "sheetProfileEntities" : qUnion([Q1]) }]});
        }
        {
            var Q0;
            Q0=qCreatedBy(id+"F1.planeOp",FACE);
            var sketch = newSketch(context, id + "F4", { "sketchPlane" : qUnion([Q0])});
            skCircle(sketch, "E23", {"center": v(0, 0) * mm, "radius": 23.71 * mm});
            skSolve(sketch);
        }
        {
            var Q0;
            Q0=qCreatedBy(makeId("Front.planeOp"),FACE);
            var sketch = newSketch(context, id + "F5", { "sketchPlane" : qUnion([Q0])});
            skCircle(sketch, "E24", {"center": v(0, 0) * mm, "radius": 35.56 * mm});
            skSolve(sketch);
        }
        {
            var Q1;
            Q1=makeQuery(id+"F4.imprint","IMPRINT",FACE,{"disambiguationData":[TD([[makeQuery(id+"F4.imprint","IMPRINT",EDGE,{"derivedFrom":sQuery(id+"F4.wireOp",EDGE,"E23")}),1.0]])]});
            var Q2;
            Q2=makeQuery(id+"F5.imprint","IMPRINT",FACE,{"disambiguationData":[TD([[makeQuery(id+"F5.imprint","IMPRINT",EDGE,{"derivedFrom":sQuery(id+"F5.wireOp",EDGE,"E24")}),1.0]])]});
            loft(context, id + "F6", {"operationType" : NewBodyOperationType.ADD, "sheetProfilesArray" : [{ "sheetProfileEntities" : qUnion([Q1]) }, { "sheetProfileEntities" : qUnion([Q2]) }]});
        }
        {
            var Q0;
            {var subQ3=sQuery(id+"F0.wireOp",EDGE,"E11.2.0");Q0=makeQuery(id+"F3.opLoft","SWEPT_BODY",BODY,{"disambiguationData":[OSD([makeQuery(id+"F0.imprint","IMPRINT",FACE,{"disambiguationData":[TD([[makeQuery(id+"F0.imprint","IMPRINT",EDGE,{"derivedFrom":subQ3}),1.0]])]}),makeQuery(id+"F2.imprint","IMPRINT",FACE,{"disambiguationData":[TD([[makeQuery(id+"F2.imprint","IMPRINT",EDGE,{"derivedFrom":sQuery(id+"F2.wireOp",EDGE,"E13.trimOffspring")}),1.0]])]})])]});}
            var Q1;
            Q1=makeQuery(id+"F6.opLoft","SWEPT_FACE",FACE,{"disambiguationData":[OSD([sQuery(id+"F4.wireOp",EDGE,"E23"),sQuery(id+"F5.wireOp",EDGE,"E24")])]});
            circularPattern(context, id + "F7", {"entities" : qUnion([Q0]), "axis" : qUnion([Q1]), "angle" : 360 * degree, "instanceCount" : 30, "equalSpace" : true});
        }
        {
            var Q0;
            {var subQ3=sQuery(id+"F0.wireOp",EDGE,"E11.2.0");Q0=makeQuery(id+"F3.opLoft","SWEPT_BODY",BODY,{"disambiguationData":[OSD([makeQuery(id+"F0.imprint","IMPRINT",FACE,{"disambiguationData":[TD([[makeQuery(id+"F0.imprint","IMPRINT",EDGE,{"derivedFrom":subQ3}),1.0]])]}),makeQuery(id+"F2.imprint","IMPRINT",FACE,{"disambiguationData":[TD([[makeQuery(id+"F2.imprint","IMPRINT",EDGE,{"derivedFrom":sQuery(id+"F2.wireOp",EDGE,"E13.trimOffspring")}),1.0]])]})])]});}
            var Q1;
            {var subQ3=sQuery(id+"F0.wireOp",EDGE,"E11.2.0");Q1=makeQuery(id+"F7.opPattern","COPY",BODY,{"derivedFrom":makeQuery(id+"F3.opLoft","SWEPT_BODY",BODY,{"disambiguationData":[OSD([makeQuery(id+"F0.imprint","IMPRINT",FACE,{"disambiguationData":[TD([[makeQuery(id+"F0.imprint","IMPRINT",EDGE,{"derivedFrom":subQ3}),1.0]])]}),makeQuery(id+"F2.imprint","IMPRINT",FACE,{"disambiguationData":[TD([[makeQuery(id+"F2.imprint","IMPRINT",EDGE,{"derivedFrom":sQuery(id+"F2.wireOp",EDGE,"E13.trimOffspring")}),1.0]])]})])]}),"instanceName":"1"});}
            var Q2;
            {var subQ3=sQuery(id+"F0.wireOp",EDGE,"E11.2.0");Q2=makeQuery(id+"F7.opPattern","COPY",BODY,{"derivedFrom":makeQuery(id+"F3.opLoft","SWEPT_BODY",BODY,{"disambiguationData":[OSD([makeQuery(id+"F0.imprint","IMPRINT",FACE,{"disambiguationData":[TD([[makeQuery(id+"F0.imprint","IMPRINT",EDGE,{"derivedFrom":subQ3}),1.0]])]}),makeQuery(id+"F2.imprint","IMPRINT",FACE,{"disambiguationData":[TD([[makeQuery(id+"F2.imprint","IMPRINT",EDGE,{"derivedFrom":sQuery(id+"F2.wireOp",EDGE,"E13.trimOffspring")}),1.0]])]})])]}),"instanceName":"2"});}
            var Q3;
            {var subQ3=sQuery(id+"F0.wireOp",EDGE,"E11.2.0");Q3=makeQuery(id+"F7.opPattern","COPY",BODY,{"derivedFrom":makeQuery(id+"F3.opLoft","SWEPT_BODY",BODY,{"disambiguationData":[OSD([makeQuery(id+"F0.imprint","IMPRINT",FACE,{"disambiguationData":[TD([[makeQuery(id+"F0.imprint","IMPRINT",EDGE,{"derivedFrom":subQ3}),1.0]])]}),makeQuery(id+"F2.imprint","IMPRINT",FACE,{"disambiguationData":[TD([[makeQuery(id+"F2.imprint","IMPRINT",EDGE,{"derivedFrom":sQuery(id+"F2.wireOp",EDGE,"E13.trimOffspring")}),1.0]])]})])]}),"instanceName":"3"});}
            var Q4;
            {var subQ3=sQuery(id+"F0.wireOp",EDGE,"E11.2.0");Q4=makeQuery(id+"F7.opPattern","COPY",BODY,{"derivedFrom":makeQuery(id+"F3.opLoft","SWEPT_BODY",BODY,{"disambiguationData":[OSD([makeQuery(id+"F0.imprint","IMPRINT",FACE,{"disambiguationData":[TD([[makeQuery(id+"F0.imprint","IMPRINT",EDGE,{"derivedFrom":subQ3}),1.0]])]}),makeQuery(id+"F2.imprint","IMPRINT",FACE,{"disambiguationData":[TD([[makeQuery(id+"F2.imprint","IMPRINT",EDGE,{"derivedFrom":sQuery(id+"F2.wireOp",EDGE,"E13.trimOffspring")}),1.0]])]})])]}),"instanceName":"4"});}
            var Q5;
            {var subQ3=sQuery(id+"F0.wireOp",EDGE,"E11.2.0");Q5=makeQuery(id+"F7.opPattern","COPY",BODY,{"derivedFrom":makeQuery(id+"F3.opLoft","SWEPT_BODY",BODY,{"disambiguationData":[OSD([makeQuery(id+"F0.imprint","IMPRINT",FACE,{"disambiguationData":[TD([[makeQuery(id+"F0.imprint","IMPRINT",EDGE,{"derivedFrom":subQ3}),1.0]])]}),makeQuery(id+"F2.imprint","IMPRINT",FACE,{"disambiguationData":[TD([[makeQuery(id+"F2.imprint","IMPRINT",EDGE,{"derivedFrom":sQuery(id+"F2.wireOp",EDGE,"E13.trimOffspring")}),1.0]])]})])]}),"instanceName":"5"});}
            var Q6;
            {var subQ3=sQuery(id+"F0.wireOp",EDGE,"E11.2.0");Q6=makeQuery(id+"F7.opPattern","COPY",BODY,{"derivedFrom":makeQuery(id+"F3.opLoft","SWEPT_BODY",BODY,{"disambiguationData":[OSD([makeQuery(id+"F0.imprint","IMPRINT",FACE,{"disambiguationData":[TD([[makeQuery(id+"F0.imprint","IMPRINT",EDGE,{"derivedFrom":subQ3}),1.0]])]}),makeQuery(id+"F2.imprint","IMPRINT",FACE,{"disambiguationData":[TD([[makeQuery(id+"F2.imprint","IMPRINT",EDGE,{"derivedFrom":sQuery(id+"F2.wireOp",EDGE,"E13.trimOffspring")}),1.0]])]})])]}),"instanceName":"6"});}
            var Q7;
            {var subQ3=sQuery(id+"F0.wireOp",EDGE,"E11.2.0");Q7=makeQuery(id+"F7.opPattern","COPY",BODY,{"derivedFrom":makeQuery(id+"F3.opLoft","SWEPT_BODY",BODY,{"disambiguationData":[OSD([makeQuery(id+"F0.imprint","IMPRINT",FACE,{"disambiguationData":[TD([[makeQuery(id+"F0.imprint","IMPRINT",EDGE,{"derivedFrom":subQ3}),1.0]])]}),makeQuery(id+"F2.imprint","IMPRINT",FACE,{"disambiguationData":[TD([[makeQuery(id+"F2.imprint","IMPRINT",EDGE,{"derivedFrom":sQuery(id+"F2.wireOp",EDGE,"E13.trimOffspring")}),1.0]])]})])]}),"instanceName":"7"});}
            var Q8;
            {var subQ3=sQuery(id+"F0.wireOp",EDGE,"E11.2.0");Q8=makeQuery(id+"F7.opPattern","COPY",BODY,{"derivedFrom":makeQuery(id+"F3.opLoft","SWEPT_BODY",BODY,{"disambiguationData":[OSD([makeQuery(id+"F0.imprint","IMPRINT",FACE,{"disambiguationData":[TD([[makeQuery(id+"F0.imprint","IMPRINT",EDGE,{"derivedFrom":subQ3}),1.0]])]}),makeQuery(id+"F2.imprint","IMPRINT",FACE,{"disambiguationData":[TD([[makeQuery(id+"F2.imprint","IMPRINT",EDGE,{"derivedFrom":sQuery(id+"F2.wireOp",EDGE,"E13.trimOffspring")}),1.0]])]})])]}),"instanceName":"8"});}
            var Q9;
            {var subQ3=sQuery(id+"F0.wireOp",EDGE,"E11.2.0");Q9=makeQuery(id+"F7.opPattern","COPY",BODY,{"derivedFrom":makeQuery(id+"F3.opLoft","SWEPT_BODY",BODY,{"disambiguationData":[OSD([makeQuery(id+"F0.imprint","IMPRINT",FACE,{"disambiguationData":[TD([[makeQuery(id+"F0.imprint","IMPRINT",EDGE,{"derivedFrom":subQ3}),1.0]])]}),makeQuery(id+"F2.imprint","IMPRINT",FACE,{"disambiguationData":[TD([[makeQuery(id+"F2.imprint","IMPRINT",EDGE,{"derivedFrom":sQuery(id+"F2.wireOp",EDGE,"E13.trimOffspring")}),1.0]])]})])]}),"instanceName":"9"});}
            var Q10;
            {var subQ3=sQuery(id+"F0.wireOp",EDGE,"E11.2.0");Q10=makeQuery(id+"F7.opPattern","COPY",BODY,{"derivedFrom":makeQuery(id+"F3.opLoft","SWEPT_BODY",BODY,{"disambiguationData":[OSD([makeQuery(id+"F0.imprint","IMPRINT",FACE,{"disambiguationData":[TD([[makeQuery(id+"F0.imprint","IMPRINT",EDGE,{"derivedFrom":subQ3}),1.0]])]}),makeQuery(id+"F2.imprint","IMPRINT",FACE,{"disambiguationData":[TD([[makeQuery(id+"F2.imprint","IMPRINT",EDGE,{"derivedFrom":sQuery(id+"F2.wireOp",EDGE,"E13.trimOffspring")}),1.0]])]})])]}),"instanceName":"10"});}
            var Q11;
            {var subQ3=sQuery(id+"F0.wireOp",EDGE,"E11.2.0");Q11=makeQuery(id+"F7.opPattern","COPY",BODY,{"derivedFrom":makeQuery(id+"F3.opLoft","SWEPT_BODY",BODY,{"disambiguationData":[OSD([makeQuery(id+"F0.imprint","IMPRINT",FACE,{"disambiguationData":[TD([[makeQuery(id+"F0.imprint","IMPRINT",EDGE,{"derivedFrom":subQ3}),1.0]])]}),makeQuery(id+"F2.imprint","IMPRINT",FACE,{"disambiguationData":[TD([[makeQuery(id+"F2.imprint","IMPRINT",EDGE,{"derivedFrom":sQuery(id+"F2.wireOp",EDGE,"E13.trimOffspring")}),1.0]])]})])]}),"instanceName":"11"});}
            var Q12;
            {var subQ3=sQuery(id+"F0.wireOp",EDGE,"E11.2.0");Q12=makeQuery(id+"F7.opPattern","COPY",BODY,{"derivedFrom":makeQuery(id+"F3.opLoft","SWEPT_BODY",BODY,{"disambiguationData":[OSD([makeQuery(id+"F0.imprint","IMPRINT",FACE,{"disambiguationData":[TD([[makeQuery(id+"F0.imprint","IMPRINT",EDGE,{"derivedFrom":subQ3}),1.0]])]}),makeQuery(id+"F2.imprint","IMPRINT",FACE,{"disambiguationData":[TD([[makeQuery(id+"F2.imprint","IMPRINT",EDGE,{"derivedFrom":sQuery(id+"F2.wireOp",EDGE,"E13.trimOffspring")}),1.0]])]})])]}),"instanceName":"12"});}
            var Q13;
            {var subQ3=sQuery(id+"F0.wireOp",EDGE,"E11.2.0");Q13=makeQuery(id+"F7.opPattern","COPY",BODY,{"derivedFrom":makeQuery(id+"F3.opLoft","SWEPT_BODY",BODY,{"disambiguationData":[OSD([makeQuery(id+"F0.imprint","IMPRINT",FACE,{"disambiguationData":[TD([[makeQuery(id+"F0.imprint","IMPRINT",EDGE,{"derivedFrom":subQ3}),1.0]])]}),makeQuery(id+"F2.imprint","IMPRINT",FACE,{"disambiguationData":[TD([[makeQuery(id+"F2.imprint","IMPRINT",EDGE,{"derivedFrom":sQuery(id+"F2.wireOp",EDGE,"E13.trimOffspring")}),1.0]])]})])]}),"instanceName":"13"});}
            var Q14;
            {var subQ3=sQuery(id+"F0.wireOp",EDGE,"E11.2.0");Q14=makeQuery(id+"F7.opPattern","COPY",BODY,{"derivedFrom":makeQuery(id+"F3.opLoft","SWEPT_BODY",BODY,{"disambiguationData":[OSD([makeQuery(id+"F0.imprint","IMPRINT",FACE,{"disambiguationData":[TD([[makeQuery(id+"F0.imprint","IMPRINT",EDGE,{"derivedFrom":subQ3}),1.0]])]}),makeQuery(id+"F2.imprint","IMPRINT",FACE,{"disambiguationData":[TD([[makeQuery(id+"F2.imprint","IMPRINT",EDGE,{"derivedFrom":sQuery(id+"F2.wireOp",EDGE,"E13.trimOffspring")}),1.0]])]})])]}),"instanceName":"14"});}
            var Q15;
            {var subQ3=sQuery(id+"F0.wireOp",EDGE,"E11.2.0");Q15=makeQuery(id+"F7.opPattern","COPY",BODY,{"derivedFrom":makeQuery(id+"F3.opLoft","SWEPT_BODY",BODY,{"disambiguationData":[OSD([makeQuery(id+"F0.imprint","IMPRINT",FACE,{"disambiguationData":[TD([[makeQuery(id+"F0.imprint","IMPRINT",EDGE,{"derivedFrom":subQ3}),1.0]])]}),makeQuery(id+"F2.imprint","IMPRINT",FACE,{"disambiguationData":[TD([[makeQuery(id+"F2.imprint","IMPRINT",EDGE,{"derivedFrom":sQuery(id+"F2.wireOp",EDGE,"E13.trimOffspring")}),1.0]])]})])]}),"instanceName":"15"});}
            var Q16;
            {var subQ3=sQuery(id+"F0.wireOp",EDGE,"E11.2.0");Q16=makeQuery(id+"F7.opPattern","COPY",BODY,{"derivedFrom":makeQuery(id+"F3.opLoft","SWEPT_BODY",BODY,{"disambiguationData":[OSD([makeQuery(id+"F0.imprint","IMPRINT",FACE,{"disambiguationData":[TD([[makeQuery(id+"F0.imprint","IMPRINT",EDGE,{"derivedFrom":subQ3}),1.0]])]}),makeQuery(id+"F2.imprint","IMPRINT",FACE,{"disambiguationData":[TD([[makeQuery(id+"F2.imprint","IMPRINT",EDGE,{"derivedFrom":sQuery(id+"F2.wireOp",EDGE,"E13.trimOffspring")}),1.0]])]})])]}),"instanceName":"16"});}
            var Q17;
            {var subQ3=sQuery(id+"F0.wireOp",EDGE,"E11.2.0");Q17=makeQuery(id+"F7.opPattern","COPY",BODY,{"derivedFrom":makeQuery(id+"F3.opLoft","SWEPT_BODY",BODY,{"disambiguationData":[OSD([makeQuery(id+"F0.imprint","IMPRINT",FACE,{"disambiguationData":[TD([[makeQuery(id+"F0.imprint","IMPRINT",EDGE,{"derivedFrom":subQ3}),1.0]])]}),makeQuery(id+"F2.imprint","IMPRINT",FACE,{"disambiguationData":[TD([[makeQuery(id+"F2.imprint","IMPRINT",EDGE,{"derivedFrom":sQuery(id+"F2.wireOp",EDGE,"E13.trimOffspring")}),1.0]])]})])]}),"instanceName":"17"});}
            var Q18;
            {var subQ3=sQuery(id+"F0.wireOp",EDGE,"E11.2.0");Q18=makeQuery(id+"F7.opPattern","COPY",BODY,{"derivedFrom":makeQuery(id+"F3.opLoft","SWEPT_BODY",BODY,{"disambiguationData":[OSD([makeQuery(id+"F0.imprint","IMPRINT",FACE,{"disambiguationData":[TD([[makeQuery(id+"F0.imprint","IMPRINT",EDGE,{"derivedFrom":subQ3}),1.0]])]}),makeQuery(id+"F2.imprint","IMPRINT",FACE,{"disambiguationData":[TD([[makeQuery(id+"F2.imprint","IMPRINT",EDGE,{"derivedFrom":sQuery(id+"F2.wireOp",EDGE,"E13.trimOffspring")}),1.0]])]})])]}),"instanceName":"18"});}
            var Q19;
            {var subQ3=sQuery(id+"F0.wireOp",EDGE,"E11.2.0");Q19=makeQuery(id+"F7.opPattern","COPY",BODY,{"derivedFrom":makeQuery(id+"F3.opLoft","SWEPT_BODY",BODY,{"disambiguationData":[OSD([makeQuery(id+"F0.imprint","IMPRINT",FACE,{"disambiguationData":[TD([[makeQuery(id+"F0.imprint","IMPRINT",EDGE,{"derivedFrom":subQ3}),1.0]])]}),makeQuery(id+"F2.imprint","IMPRINT",FACE,{"disambiguationData":[TD([[makeQuery(id+"F2.imprint","IMPRINT",EDGE,{"derivedFrom":sQuery(id+"F2.wireOp",EDGE,"E13.trimOffspring")}),1.0]])]})])]}),"instanceName":"19"});}
            var Q20;
            {var subQ3=sQuery(id+"F0.wireOp",EDGE,"E11.2.0");Q20=makeQuery(id+"F7.opPattern","COPY",BODY,{"derivedFrom":makeQuery(id+"F3.opLoft","SWEPT_BODY",BODY,{"disambiguationData":[OSD([makeQuery(id+"F0.imprint","IMPRINT",FACE,{"disambiguationData":[TD([[makeQuery(id+"F0.imprint","IMPRINT",EDGE,{"derivedFrom":subQ3}),1.0]])]}),makeQuery(id+"F2.imprint","IMPRINT",FACE,{"disambiguationData":[TD([[makeQuery(id+"F2.imprint","IMPRINT",EDGE,{"derivedFrom":sQuery(id+"F2.wireOp",EDGE,"E13.trimOffspring")}),1.0]])]})])]}),"instanceName":"20"});}
            var Q21;
            {var subQ3=sQuery(id+"F0.wireOp",EDGE,"E11.2.0");Q21=makeQuery(id+"F7.opPattern","COPY",BODY,{"derivedFrom":makeQuery(id+"F3.opLoft","SWEPT_BODY",BODY,{"disambiguationData":[OSD([makeQuery(id+"F0.imprint","IMPRINT",FACE,{"disambiguationData":[TD([[makeQuery(id+"F0.imprint","IMPRINT",EDGE,{"derivedFrom":subQ3}),1.0]])]}),makeQuery(id+"F2.imprint","IMPRINT",FACE,{"disambiguationData":[TD([[makeQuery(id+"F2.imprint","IMPRINT",EDGE,{"derivedFrom":sQuery(id+"F2.wireOp",EDGE,"E13.trimOffspring")}),1.0]])]})])]}),"instanceName":"21"});}
            var Q22;
            {var subQ3=sQuery(id+"F0.wireOp",EDGE,"E11.2.0");Q22=makeQuery(id+"F7.opPattern","COPY",BODY,{"derivedFrom":makeQuery(id+"F3.opLoft","SWEPT_BODY",BODY,{"disambiguationData":[OSD([makeQuery(id+"F0.imprint","IMPRINT",FACE,{"disambiguationData":[TD([[makeQuery(id+"F0.imprint","IMPRINT",EDGE,{"derivedFrom":subQ3}),1.0]])]}),makeQuery(id+"F2.imprint","IMPRINT",FACE,{"disambiguationData":[TD([[makeQuery(id+"F2.imprint","IMPRINT",EDGE,{"derivedFrom":sQuery(id+"F2.wireOp",EDGE,"E13.trimOffspring")}),1.0]])]})])]}),"instanceName":"22"});}
            var Q23;
            {var subQ3=sQuery(id+"F0.wireOp",EDGE,"E11.2.0");Q23=makeQuery(id+"F7.opPattern","COPY",BODY,{"derivedFrom":makeQuery(id+"F3.opLoft","SWEPT_BODY",BODY,{"disambiguationData":[OSD([makeQuery(id+"F0.imprint","IMPRINT",FACE,{"disambiguationData":[TD([[makeQuery(id+"F0.imprint","IMPRINT",EDGE,{"derivedFrom":subQ3}),1.0]])]}),makeQuery(id+"F2.imprint","IMPRINT",FACE,{"disambiguationData":[TD([[makeQuery(id+"F2.imprint","IMPRINT",EDGE,{"derivedFrom":sQuery(id+"F2.wireOp",EDGE,"E13.trimOffspring")}),1.0]])]})])]}),"instanceName":"23"});}
            var Q24;
            {var subQ3=sQuery(id+"F0.wireOp",EDGE,"E11.2.0");Q24=makeQuery(id+"F7.opPattern","COPY",BODY,{"derivedFrom":makeQuery(id+"F3.opLoft","SWEPT_BODY",BODY,{"disambiguationData":[OSD([makeQuery(id+"F0.imprint","IMPRINT",FACE,{"disambiguationData":[TD([[makeQuery(id+"F0.imprint","IMPRINT",EDGE,{"derivedFrom":subQ3}),1.0]])]}),makeQuery(id+"F2.imprint","IMPRINT",FACE,{"disambiguationData":[TD([[makeQuery(id+"F2.imprint","IMPRINT",EDGE,{"derivedFrom":sQuery(id+"F2.wireOp",EDGE,"E13.trimOffspring")}),1.0]])]})])]}),"instanceName":"24"});}
            var Q25;
            {var subQ3=sQuery(id+"F0.wireOp",EDGE,"E11.2.0");Q25=makeQuery(id+"F7.opPattern","COPY",BODY,{"derivedFrom":makeQuery(id+"F3.opLoft","SWEPT_BODY",BODY,{"disambiguationData":[OSD([makeQuery(id+"F0.imprint","IMPRINT",FACE,{"disambiguationData":[TD([[makeQuery(id+"F0.imprint","IMPRINT",EDGE,{"derivedFrom":subQ3}),1.0]])]}),makeQuery(id+"F2.imprint","IMPRINT",FACE,{"disambiguationData":[TD([[makeQuery(id+"F2.imprint","IMPRINT",EDGE,{"derivedFrom":sQuery(id+"F2.wireOp",EDGE,"E13.trimOffspring")}),1.0]])]})])]}),"instanceName":"25"});}
            var Q26;
            {var subQ3=sQuery(id+"F0.wireOp",EDGE,"E11.2.0");Q26=makeQuery(id+"F7.opPattern","COPY",BODY,{"derivedFrom":makeQuery(id+"F3.opLoft","SWEPT_BODY",BODY,{"disambiguationData":[OSD([makeQuery(id+"F0.imprint","IMPRINT",FACE,{"disambiguationData":[TD([[makeQuery(id+"F0.imprint","IMPRINT",EDGE,{"derivedFrom":subQ3}),1.0]])]}),makeQuery(id+"F2.imprint","IMPRINT",FACE,{"disambiguationData":[TD([[makeQuery(id+"F2.imprint","IMPRINT",EDGE,{"derivedFrom":sQuery(id+"F2.wireOp",EDGE,"E13.trimOffspring")}),1.0]])]})])]}),"instanceName":"26"});}
            var Q27;
            {var subQ3=sQuery(id+"F0.wireOp",EDGE,"E11.2.0");Q27=makeQuery(id+"F7.opPattern","COPY",BODY,{"derivedFrom":makeQuery(id+"F3.opLoft","SWEPT_BODY",BODY,{"disambiguationData":[OSD([makeQuery(id+"F0.imprint","IMPRINT",FACE,{"disambiguationData":[TD([[makeQuery(id+"F0.imprint","IMPRINT",EDGE,{"derivedFrom":subQ3}),1.0]])]}),makeQuery(id+"F2.imprint","IMPRINT",FACE,{"disambiguationData":[TD([[makeQuery(id+"F2.imprint","IMPRINT",EDGE,{"derivedFrom":sQuery(id+"F2.wireOp",EDGE,"E13.trimOffspring")}),1.0]])]})])]}),"instanceName":"27"});}
            var Q28;
            {var subQ3=sQuery(id+"F0.wireOp",EDGE,"E11.2.0");Q28=makeQuery(id+"F7.opPattern","COPY",BODY,{"derivedFrom":makeQuery(id+"F3.opLoft","SWEPT_BODY",BODY,{"disambiguationData":[OSD([makeQuery(id+"F0.imprint","IMPRINT",FACE,{"disambiguationData":[TD([[makeQuery(id+"F0.imprint","IMPRINT",EDGE,{"derivedFrom":subQ3}),1.0]])]}),makeQuery(id+"F2.imprint","IMPRINT",FACE,{"disambiguationData":[TD([[makeQuery(id+"F2.imprint","IMPRINT",EDGE,{"derivedFrom":sQuery(id+"F2.wireOp",EDGE,"E13.trimOffspring")}),1.0]])]})])]}),"instanceName":"28"});}
            var Q29;
            {var subQ3=sQuery(id+"F0.wireOp",EDGE,"E11.2.0");Q29=makeQuery(id+"F7.opPattern","COPY",BODY,{"derivedFrom":makeQuery(id+"F3.opLoft","SWEPT_BODY",BODY,{"disambiguationData":[OSD([makeQuery(id+"F0.imprint","IMPRINT",FACE,{"disambiguationData":[TD([[makeQuery(id+"F0.imprint","IMPRINT",EDGE,{"derivedFrom":subQ3}),1.0]])]}),makeQuery(id+"F2.imprint","IMPRINT",FACE,{"disambiguationData":[TD([[makeQuery(id+"F2.imprint","IMPRINT",EDGE,{"derivedFrom":sQuery(id+"F2.wireOp",EDGE,"E13.trimOffspring")}),1.0]])]})])]}),"instanceName":"29"});}
            booleanBodies(context, id + "F8", {"operationType" : BooleanOperationType.UNION, "tools" : qUnion([Q0, Q1, Q2, Q3, Q4, Q5, Q6, Q7, Q8, Q9, Q10, Q11, Q12, Q13, Q14, Q15, Q16, Q17, Q18, Q19, Q20, Q21, Q22, Q23, Q24, Q25, Q26, Q27, Q28, Q29])});
        }
        {
            var Q0;
            {var subQ3=makeQuery(id+"F6.boolean.opBoolean","MERGE",FACE,{"derivedFrom":[makeQuery(id+"F3.opLoft","CAP_FACE",FACE,{"disambiguationData":[OSD([makeQuery(id+"F2.imprint","IMPRINT",FACE,{"disambiguationData":[TD([[makeQuery(id+"F2.imprint","IMPRINT",EDGE,{"derivedFrom":sQuery(id+"F2.wireOp",EDGE,"E13.trimOffspring")}),1.0]])]})])],"isStart":true}),makeQuery(id+"F6.opLoft","CAP_FACE",FACE,{"disambiguationData":[OSD([makeQuery(id+"F4.imprint","IMPRINT",FACE,{"disambiguationData":[TD([[makeQuery(id+"F4.imprint","IMPRINT",EDGE,{"derivedFrom":sQuery(id+"F4.wireOp",EDGE,"E23")}),1.0]])]})])],"isStart":true})]});Q0=makeQuery(id+"F8.opBoolean","MERGE",FACE,{"derivedFrom":[subQ3,makeQuery(id+"F7.opPattern","COPY",FACE,{"derivedFrom":subQ3,"instanceName":"1"}),makeQuery(id+"F7.opPattern","COPY",FACE,{"derivedFrom":subQ3,"instanceName":"2"}),makeQuery(id+"F7.opPattern","COPY",FACE,{"derivedFrom":subQ3,"instanceName":"3"}),makeQuery(id+"F7.opPattern","COPY",FACE,{"derivedFrom":subQ3,"instanceName":"4"}),makeQuery(id+"F7.opPattern","COPY",FACE,{"derivedFrom":subQ3,"instanceName":"5"}),makeQuery(id+"F7.opPattern","COPY",FACE,{"derivedFrom":subQ3,"instanceName":"6"}),makeQuery(id+"F7.opPattern","COPY",FACE,{"derivedFrom":subQ3,"instanceName":"7"}),makeQuery(id+"F7.opPattern","COPY",FACE,{"derivedFrom":subQ3,"instanceName":"8"}),makeQuery(id+"F7.opPattern","COPY",FACE,{"derivedFrom":subQ3,"instanceName":"9"}),makeQuery(id+"F7.opPattern","COPY",FACE,{"derivedFrom":subQ3,"instanceName":"10"}),makeQuery(id+"F7.opPattern","COPY",FACE,{"derivedFrom":subQ3,"instanceName":"11"}),makeQuery(id+"F7.opPattern","COPY",FACE,{"derivedFrom":subQ3,"instanceName":"12"}),makeQuery(id+"F7.opPattern","COPY",FACE,{"derivedFrom":subQ3,"instanceName":"13"}),makeQuery(id+"F7.opPattern","COPY",FACE,{"derivedFrom":subQ3,"instanceName":"14"}),makeQuery(id+"F7.opPattern","COPY",FACE,{"derivedFrom":subQ3,"instanceName":"15"}),makeQuery(id+"F7.opPattern","COPY",FACE,{"derivedFrom":subQ3,"instanceName":"16"}),makeQuery(id+"F7.opPattern","COPY",FACE,{"derivedFrom":subQ3,"instanceName":"17"}),makeQuery(id+"F7.opPattern","COPY",FACE,{"derivedFrom":subQ3,"instanceName":"18"}),makeQuery(id+"F7.opPattern","COPY",FACE,{"derivedFrom":subQ3,"instanceName":"19"}),makeQuery(id+"F7.opPattern","COPY",FACE,{"derivedFrom":subQ3,"instanceName":"20"}),makeQuery(id+"F7.opPattern","COPY",FACE,{"derivedFrom":subQ3,"instanceName":"21"}),makeQuery(id+"F7.opPattern","COPY",FACE,{"derivedFrom":subQ3,"instanceName":"22"}),makeQuery(id+"F7.opPattern","COPY",FACE,{"derivedFrom":subQ3,"instanceName":"23"}),makeQuery(id+"F7.opPattern","COPY",FACE,{"derivedFrom":subQ3,"instanceName":"24"}),makeQuery(id+"F7.opPattern","COPY",FACE,{"derivedFrom":subQ3,"instanceName":"25"}),makeQuery(id+"F7.opPattern","COPY",FACE,{"derivedFrom":subQ3,"instanceName":"26"}),makeQuery(id+"F7.opPattern","COPY",FACE,{"derivedFrom":subQ3,"instanceName":"27"}),makeQuery(id+"F7.opPattern","COPY",FACE,{"derivedFrom":subQ3,"instanceName":"28"}),makeQuery(id+"F7.opPattern","COPY",FACE,{"derivedFrom":subQ3,"instanceName":"29"})]});}
            var sketch = newSketch(context, id + "F9", { "sketchPlane" : qUnion([Q0])});
            skCircle(sketch, "E25", {"center": v(0, 0) * mm, "radius": 6.35 * mm});
            skSolve(sketch);
        }
        {
            var Q0;
            Q0 = qSketchRegion(id + "F9", true);
            extrude(context, id + "F10", {"entities" : qUnion([Q0]), "operationType" : NewBodyOperationType.REMOVE, "endBound" : BoundingType.THROUGH_ALL, "oppositeDirection" : true, "depth" : 25.4 * mm});
        }
    });
